# Revit family: HARMANN -Tłumik_Akustyczny-Harmann-SDQ_100_315
name_source: partatom
category: Akcesoria wentylacyjne
units: mm (PartAtom-declared; Revit-internal decimal feet)

## family parameters
Oparty na płaszczyźnie roboczej = Nie
Tnij formami wycięć po wczytaniu = Nie
Typ części = Dzieli na
Współdzielony = Nie
Wymiar okrągłego złącza = Użyj średnicy
Zawsze pionowo = Tak

## types (18) — shared parameters
Domyślna rzędna = 0.0 mm
IfcExportAs = IfcDuctSilencerType
IfcExportType = ROUND
Kod Producent = Harmann
Kod Typoszereg = SDQ
Object Date = 2020.12.29
Object Destination = PL
Object ID = F001102RFAPL
Object Language = PL
Object Revit = 2018
Object Version = 1.00
Otoczenie Temperatura Maksymalna = 60.0 °C
Otoczenie Temperatura Minimalna = -25.0 °C
Powietrze Gęstość Nominalna = 1.2000 kg/m³
Powietrze Temperatura Maksymalna = 60.0 °C
Powietrze Temperatura Minimalna = -25.0 °C
Producent = Harmann Polska Sp. z o.o.
Producent Nazwa = Harmann Polska Sp. z o.o.
Prt Komponent N1 = VE-Komponent-ParaForma-Harmann-SDS-N1a : Harmann
Systematyka Branża = Instalacje Sanitarne
Systematyka Dziedzina = Instalacje Wentylacyjne
Systematyka Klasa = Akcesorium
Systematyka Rodzaj = Tłumik Akustyczny
nr_n1 = 1

## per-type parameters (varying)
| type | Kod Numer Katalogowy | Kod Zamówienia | Masa Netto | Model | Opis | Opis indeksowy | Powietrze Powierzchnia Czynna | Powietrze Przepływ Maksymalny | Powietrze Przepływ Minimalny | Powietrze Przepływ Nominalny | Powietrze Strata Ciśnienia Nominalna | Powietrze Współczynnik ζ | dn | l1_a0 | l2_a0 | nr | s1_d0 | s1_l1 | s1_l2 |
| 100-0600 | 20411100 | SDQ 100-600 | 3.0 kg | SDQ 100-600 | Tłumik akustyczny sztywny | SDQ 100-600 | 0.0079 m² | 160 m³/h | 10 m³/h | 100 m³/h | 1.5 Pa | 0.15 | 100.0 mm | 300.0 mm | 300.0 mm | 1 | 200.0 mm | 300.0 mm | 300.0 mm |
| 100-0900 | 20412100 | SDQ 100-900 | 5.0 kg | SDQ 100-900 | Tłumik akustyczny sztywny | SDQ 100-900 | 0.0079 m² | 160 m³/h | 10 m³/h | 100 m³/h | 1.6 Pa | 0.16 | 100.0 mm | 450.0 mm | 450.0 mm | 2 | 200.0 mm | 450.0 mm | 450.0 mm |
| 100-1200 | 20413100 | SDQ 100-1200 | 7.0 kg | SDQ 100-1200 | Tłumik akustyczny sztywny | SDQ 100-1200 | 0.0079 m² | 160 m³/h | 10 m³/h | 100 m³/h | 1.7 Pa | 0.28 | 100.0 mm | 600.0 mm | 600.0 mm | 3 | 200.0 mm | 600.0 mm | 600.0 mm |
| 125-0600 | 20411125 | SDQ 125-600 | 4.0 kg | SDQ 125-600 | Tłumik akustyczny sztywny | SDQ 125-600 | 0.0123 m² | 250 m³/h | 15 m³/h | 150 m³/h | 1.0 Pa | 0.12 | 125.0 mm | 300.0 mm | 300.0 mm | 1 | 200.0 mm | 300.0 mm | 300.0 mm |
| 125-0900 | 20412125 | SDQ 125-900 | 7.0 kg | SDQ 125-900 | Tłumik akustyczny sztywny | SDQ 125-900 | 0.0123 m² | 250 m³/h | 15 m³/h | 150 m³/h | 1.2 Pa | 0.14 | 125.0 mm | 450.0 mm | 450.0 mm | 2 | 224.0 mm | 450.0 mm | 450.0 mm |
| 125-1200 | 20413125 | SDQ 125-1200 | 9.0 kg | SDQ 125-1200 | Tłumik akustyczny sztywny | SDQ 125-1200 | 0.0123 m² | 250 m³/h | 15 m³/h | 150 m³/h | 1.4 Pa | 0.21 | 125.0 mm | 600.0 mm | 600.0 mm | 3 | 224.0 mm | 600.0 mm | 600.0 mm |
| 160-0600 | 20411160 | SDQ 160-600 | 6.0 kg | SDQ 160-600 | Tłumik akustyczny sztywny | SDQ 160-600 | 0.0201 m² | 400 m³/h | 20 m³/h | 250 m³/h | 1.0 Pa | 0.1 | 160.0 mm | 300.0 mm | 300.0 mm | 1 | 260.0 mm | 300.0 mm | 300.0 mm |
| 160-0900 | 20412160 | SDQ 160-900 | 8.0 kg |  |  |  | 0.0201 m² | 400 m³/h | 20 m³/h | 250 m³/h | 1.1 Pa | 0.11 | 160.0 mm | 450.0 mm | 450.0 mm | 2 | 260.0 mm | 450.0 mm | 450.0 mm |
| 160-1200 | 20413160 | SDQ 160-1200 | 10.0 kg | SDQ 160-1200 | Tłumik akustyczny sztywny | SDQ 160-1200 | 0.0201 m² | 400 m³/h | 20 m³/h | 250 m³/h | 1.3 Pa | 0.2 | 160.0 mm | 600.0 mm | 600.0 mm | 3 | 260.0 mm | 600.0 mm | 600.0 mm |
| 200-0600 | 20411200 | SDQ 200-600 | 7.0 kg | SDQ 200-600 | Tłumik akustyczny sztywny | SDQ 200-600 | 0.0314 m² | 650 m³/h | 30 m³/h | 400 m³/h | 0.7 Pa | 0.08 | 200.0 mm | 300.0 mm | 300.0 mm | 1 | 315.0 mm | 300.0 mm | 300.0 mm |
| 200-0900 | 20412200 | SDQ 200-900 | 10.0 kg | SDQ 200-900 | Tłumik akustyczny sztywny | SDQ 200-900 | 0.0314 m² | 650 m³/h | 30 m³/h | 400 m³/h | 0.8 Pa | 0.09 | 200.0 mm | 450.0 mm | 450.0 mm | 2 | 315.0 mm | 450.0 mm | 450.0 mm |
| 200-1200 | 20413200 | SDQ 200-1200 | 12.0 kg | SDQ 200-1200 | Tłumik akustyczny sztywny | SDQ 200-1200 | 0.0314 m² | 650 m³/h | 30 m³/h | 400 m³/h | 1.0 Pa | 1.6 | 200.0 mm | 600.0 mm | 600.0 mm | 3 | 315.0 mm | 600.0 mm | 600.0 mm |
| 250-0600 | 20411250 | SDQ 250-600 | 9.0 kg | SDQ 250-600 | Tłumik akustyczny sztywny | SDQ 250-600 | 0.0491 m² | 1000 m³/h | 50 m³/h | 600 m³/h | 0.7 Pa | 0.08 | 250.0 mm | 300.0 mm | 300.0 mm | 1 | 355.0 mm | 300.0 mm | 300.0 mm |
| 250-0900 | 20412250 | SDQ 250-900 | 12.0 kg | SDQ 250-900 | Tłumik akustyczny sztywny | SDQ 250-900 | 0.0491 m² | 1000 m³/h | 50 m³/h | 600 m³/h | 0.8 Pa | 0.09 | 250.0 mm | 450.0 mm | 450.0 mm | 2 | 355.0 mm | 450.0 mm | 450.0 mm |
| 250-1200 | 20413250 | SDQ 250-1200 | 15.0 kg | SDQ 250-1200 | Tłumik akustyczny sztywny | SDQ 250-1200 | 0.0491 m² | 1000 m³/h | 50 m³/h | 600 m³/h | 1.0 Pa | 0.14 | 250.0 mm | 600.0 mm | 600.0 mm | 3 | 355.0 mm | 600.0 mm | 600.0 mm |
| 315-0600 | 20411315 | SDQ 315-600 | 12.0 kg | SDQ 315-600 | Tłumik akustyczny sztywny | SDQ 315-600 | 0.0779 m² | 1600 m³/h | 80 m³/h | 1000 m³/h | 0.6 Pa | 0.055 | 315.0 mm | 300.0 mm | 300.0 mm | 1 | 500.0 mm | 300.0 mm | 300.0 mm |
| 315-0900 | 20412315 | SDQ 315-900 | 18.0 kg | SDQ 315-900 | Tłumik akustyczny sztywny | SDQ 315-900 | 0.0779 m² | 1600 m³/h | 80 m³/h | 1000 m³/h | 0.7 Pa | 0.07 | 315.0 mm | 450.0 mm | 450.0 mm | 2 | 500.0 mm | 450.0 mm | 450.0 mm |
| 315-1200 | 20413315
20413315 | SDQ 315-1200 | 18.0 kg | SDQ 315-1200 | Tłumik akustyczny sztywny | SDQ 315-1200 | 0.0779 m² | 1600 m³/h | 80 m³/h | 1000 m³/h | 1.1 Pa | 0.12 | 315.0 mm | 600.0 mm | 600.0 mm | 3 | 500.0 mm | 600.0 mm | 600.0 mm |
